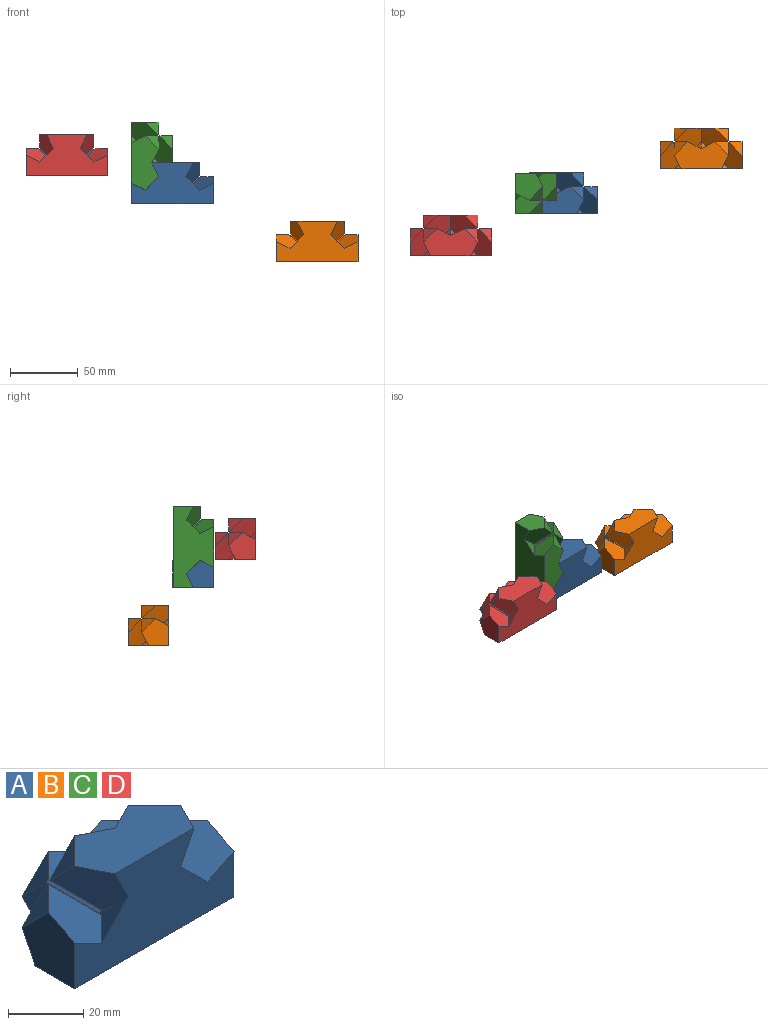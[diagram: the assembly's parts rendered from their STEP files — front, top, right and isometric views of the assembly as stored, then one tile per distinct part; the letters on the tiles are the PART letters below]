
ASSEMBLY  parts=4 mates=1
PART A: 36 faces, bbox 60x30x30 mm
  f0: plane 10.75x10.75mm, normal (-0.41,0.41,-0.82), area 17.4mm2, adj f4,f5,f12,f13
  f1: plane 10.75x10.75mm, normal (0.41,0.41,-0.82), area 17.4mm2, adj f3,f8,f15,f21
  f2: plane 10.75x10.75mm, normal (-0.82,0.41,0.41), area 17.4mm2, adj f6,f11,f17,f22
  f3: plane 9.88x9.88mm, normal (0.58,0.58,0.58), area 84.1mm2, adj f1,f8,f14,f15
  f4: plane 19.23x19.21mm, normal (0.41,0.82,-0.41), area 287.6mm2, adj f0,f5,f8,f12,f14
  f5: plane 9.88x9.88mm, normal (-0.58,0.58,0.58), area 84.1mm2, adj f0,f4,f13,f14
  f6: plane 10.79x9.9mm, normal (0.58,0.58,0.58), area 0.5mm2, adj f2,f16,f21
  f7: plane 10.75x10.75mm, normal (0.82,0.41,0.41), area 17.4mm2, adj f18,f19,f20,f26
  f8: plane 19.23x19.21mm, normal (-0.41,0.82,-0.41), area 287.6mm2, adj f1,f3,f4,f14,f21
  f9: plane 10.75x10.75mm, normal (-0.41,-0.82,0.41), area 17.4mm2, adj f12,f28,f31,f32
  f10: plane 10.75x10.75mm, normal (0.41,-0.82,0.41), area 17.4mm2, adj f21,f29,f30,f35
  f11: plane 9.88x9.88mm, normal (0.58,0.58,0.58), area 84.1mm2, adj f2,f17,f22,f23
  f12: plane 19.97x19.97mm, normal (-0.58,0.58,0.58), area 177.3mm2, adj f0,f4,f9,f13,f18,f20,f21,f24
  f13: plane 19.23x19.21mm, normal (-0.82,-0.41,-0.41), area 287.6mm2, adj f0,f5,f12,f14,f24
  f14: plane 39.88x19.94mm, normal (0,0,1), area 596.3mm2, adj f3,f4,f5,f8,f13,f15,f24
  f15: plane 19.23x19.21mm, normal (0.82,-0.41,-0.41), area 287.6mm2, adj f1,f3,f14,f21,f24
  f16: plane 10.08x10.08mm, normal (0.58,0.58,0.58), area 80.2mm2, adj f6,f17,f24
  f17: plane 19.23x19.21mm, normal (-0.41,-0.41,0.82), area 287.6mm2, adj f2,f11,f16,f23,f24
  f18: plane 19.23x19.21mm, normal (0.41,-0.41,0.82), area 287.6mm2, adj f7,f12,f19,f24,f25
  f19: plane 9.88x9.88mm, normal (-0.58,0.58,0.58), area 84.1mm2, adj f7,f18,f25,f26
  f20: plane 10.79x9.9mm, normal (-0.58,0.58,0.58), area 7.6mm2, adj f7,f12,f27,f31
  f21: plane 19.97x19.97mm, normal (0.58,0.58,0.58), area 184.4mm2, adj f1,f6,f8,f10,f12,f15,f22,f29
  f22: plane 19.23x19.21mm, normal (-0.41,0.82,-0.41), area 287.6mm2, adj f2,f11,f21,f23,f33
  f23: plane 19.94x19.94mm, normal (1,0,0), area 298.2mm2, adj f11,f17,f22,f24,f33
  f24: plane 60x30mm, normal (0,-1,0), area 1193.7mm2, adj f12,f13,f14,f15,f16,f17,f18,f23
  f25: plane 19.94x19.94mm, normal (-1,0,0), area 298.2mm2, adj f18,f19,f24,f26,f33
  f26: plane 19.23x19.21mm, normal (0.41,0.82,-0.41), area 287.6mm2, adj f7,f19,f25,f27,f33
  f27: plane 10.08x10.08mm, normal (-0.58,0.58,0.58), area 80.2mm2, adj f20,f26,f33
  f28: plane 19.23x19.21mm, normal (0.41,-0.41,0.82), area 287.6mm2, adj f9,f12,f29,f32,f34
  f29: plane 19.23x19.21mm, normal (-0.41,-0.41,0.82), area 287.6mm2, adj f10,f21,f28,f30,f34
  f30: plane 9.88x9.88mm, normal (0.58,0.58,0.58), area 84.1mm2, adj f10,f29,f34,f35
  f31: plane 19.23x19.21mm, normal (-0.82,-0.41,-0.41), area 287.6mm2, adj f9,f20,f32,f33,f34
  f32: plane 9.88x9.88mm, normal (-0.58,0.58,0.58), area 84.1mm2, adj f9,f28,f31,f34
  f33: plane 60x30mm, normal (0,0,-1), area 1193.7mm2, adj f21,f22,f23,f24,f25,f26,f27,f31
  f34: plane 39.88x19.94mm, normal (0,1,0), area 596.3mm2, adj f28,f29,f30,f31,f32,f33,f35
  f35: plane 19.23x19.21mm, normal (0.82,-0.41,-0.41), area 287.6mm2, adj f10,f21,f30,f33,f34
PART B: same geometry as A
PART C: same geometry as A
PART D: same geometry as A
PLACE A t=(4.71,-13.94,15.19)mm
PLACE B t=(111.21,19.05,-27.57)mm
PLACE C rot(axis=(0.58,0.58,-0.58),120deg) t=(-40.29,0.88,15.19)mm
PLACE D t=(-73,-44.96,35.95)mm
MATE fastened C.f24 <-> A.f25  axis (-1,0,0) through (-40.29,0.97,0.19)mm
